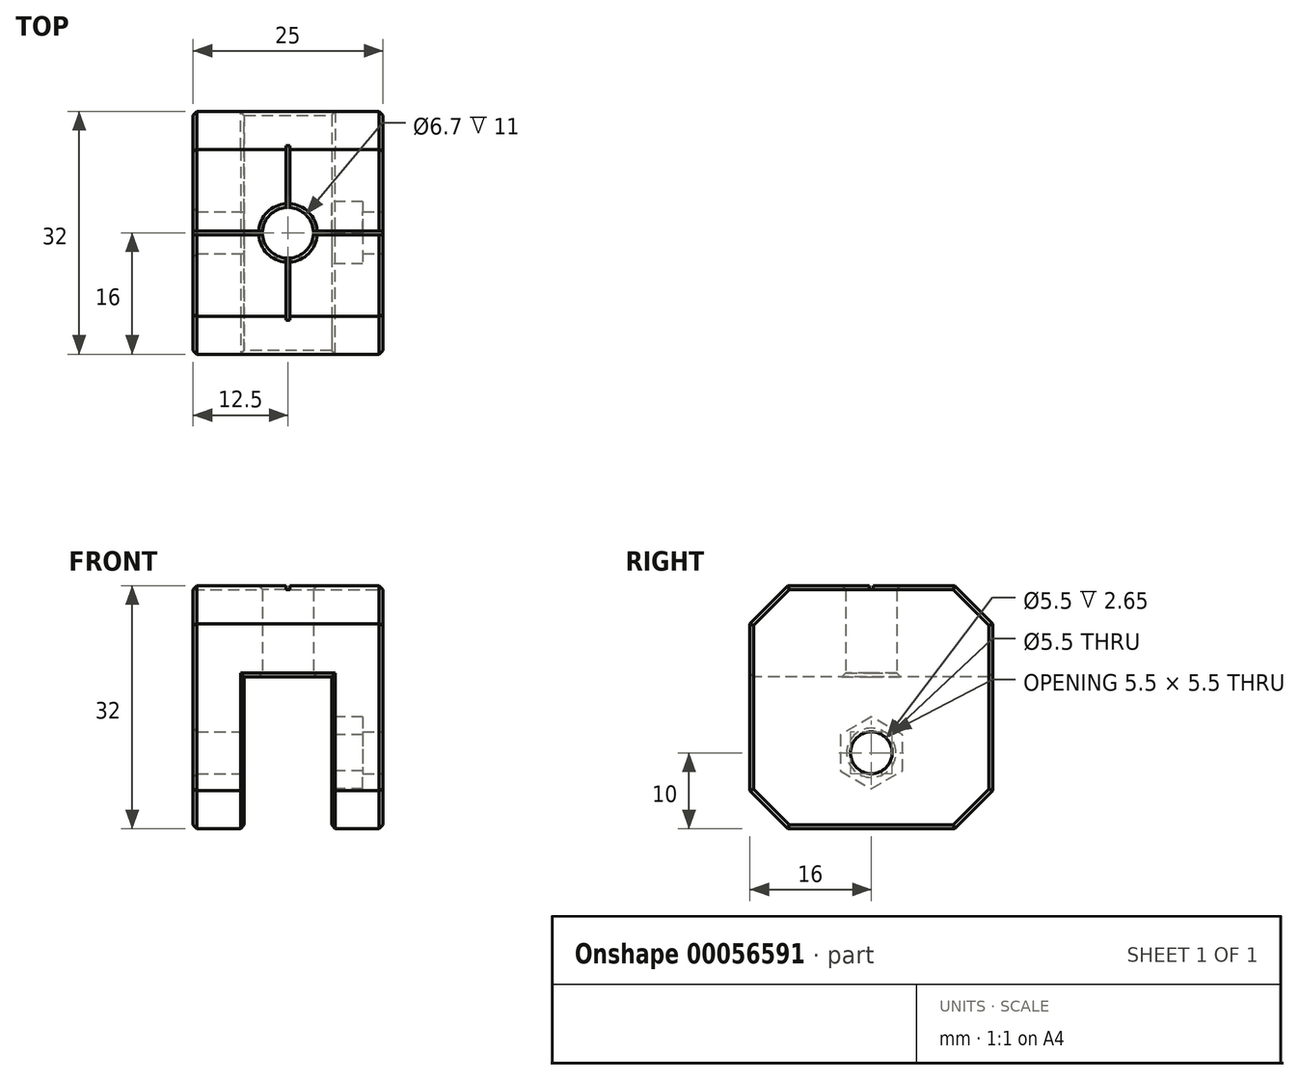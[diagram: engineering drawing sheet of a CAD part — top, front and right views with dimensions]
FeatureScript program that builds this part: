
annotation { "Feature Type Name" : "Feature", "Feature Type Description" : "" }
export const myFeature = defineFeature(function(context is Context, id is Id, definition is map)
    precondition{}
    {
        {
            var Q0;
            Q0=qCreatedBy(makeId("Top.planeOp"),FACE);
            var sketch = newSketch(context, id + "F0", { "sketchPlane" : qUnion([Q0])});
            skCircle(sketch, "E0", {"center": v(0, 0) * mm, "radius": 3.35 * mm});
            skLineSegment(sketch, "E1.bottom", {"start": v(12.5, 16) * mm, "end": v(-12.5, 16) * mm});
            skLineSegment(sketch, "E1.top", {"start": v(12.5, -16) * mm, "end": v(-12.5, -16) * mm});
            skLineSegment(sketch, "E1.left", {"start": v(12.5, 16) * mm, "end": v(12.5, -16) * mm});
            skLineSegment(sketch, "E1.right", {"start": v(-12.5, 16) * mm, "end": v(-12.5, -16) * mm});
            skLineSegment(sketch, "E2", {"start": v(5.75, 16) * mm, "end": v(5.75, -16) * mm});
            skLineSegment(sketch, "E3", {"start": v(-5.75, 16) * mm, "end": v(-5.75, -16) * mm});
            skLineSegment(sketch, "E4", {"start": v(12.5, 0) * mm, "end": v(5.75, 0) * mm, "construction": true});
            skLineSegment(sketch, "E5", {"start": v(5.75, 0) * mm, "end": v(0, 0) * mm, "construction": true});
            skLineSegment(sketch, "E6", {"start": v(-5.75, 0) * mm, "end": v(0, 0) * mm, "construction": true});
            skLineSegment(sketch, "E7", {"start": v(-5.75, 0) * mm, "end": v(-12.5, 0) * mm, "construction": true});
            skSolve(sketch);
        }
        {
            var Q0;
            Q0 = qSketchRegion(id + "F0", true);
            extrude(context, id + "F1", {"entities" : qUnion([Q0]), "depth" : 12 * mm});
        }
        {
            var Q0;
            {var subQ0=sQuery(id+"F0.wireOp",EDGE,"E1.left");Q0=makeQuery(id+"F0.imprint","IMPRINT",FACE,{"disambiguationData":[TD([[makeQuery(id+"F0.imprint","IMPRINT",EDGE,{"derivedFrom":subQ0}),-1.0]])]});}
            var Q1;
            {var subQ0=sQuery(id+"F0.wireOp",EDGE,"E1.right");Q1=makeQuery(id+"F0.imprint","IMPRINT",FACE,{"disambiguationData":[TD([[makeQuery(id+"F0.imprint","IMPRINT",EDGE,{"derivedFrom":subQ0}),1.0]])]});}
            extrude(context, id + "F2", {"entities" : qUnion([Q0, Q1]), "operationType" : NewBodyOperationType.ADD, "oppositeDirection" : true, "depth" : 20 * mm});
        }
        {
            var Q0;
            {var subQ0=sQuery(id+"F0.wireOp",EDGE,"E1.top");Q0=makeQuery(id+"F2.opExtrude","CAP_EDGE",EDGE,{"disambiguationData":[OSD([subQ0]),TDD([makeQuery(id+"F0.imprint","IMPRINT",EDGE,{"disambiguationData":[TD([[makeQuery(id+"F0.imprint","INTERSECT",VERTEX,{"derivedFrom":[subQ0,sQuery(id+"F0.wireOp",EDGE,"E1.right")]}),1.0]])],"derivedFrom":subQ0})])],"isStart":false});}
            var Q1;
            {var subQ0=sQuery(id+"F0.wireOp",EDGE,"E1.top");Q1=makeQuery(id+"F2.opExtrude","CAP_EDGE",EDGE,{"disambiguationData":[OSD([subQ0]),TDD([makeQuery(id+"F0.imprint","IMPRINT",EDGE,{"disambiguationData":[TD([[makeQuery(id+"F0.imprint","INTERSECT",VERTEX,{"derivedFrom":[subQ0,sQuery(id+"F0.wireOp",EDGE,"E1.left")]}),-1.0]])],"derivedFrom":subQ0})])],"isStart":false});}
            var Q2;
            {var subQ0=sQuery(id+"F0.wireOp",EDGE,"E1.bottom");Q2=makeQuery(id+"F2.opExtrude","CAP_EDGE",EDGE,{"disambiguationData":[OSD([subQ0]),TDD([makeQuery(id+"F0.imprint","IMPRINT",EDGE,{"disambiguationData":[TD([[makeQuery(id+"F0.imprint","INTERSECT",VERTEX,{"derivedFrom":[subQ0,sQuery(id+"F0.wireOp",EDGE,"E1.left")]}),-1.0]])],"derivedFrom":subQ0})])],"isStart":false});}
            var Q3;
            {var subQ0=sQuery(id+"F0.wireOp",EDGE,"E1.bottom");Q3=makeQuery(id+"F2.opExtrude","CAP_EDGE",EDGE,{"disambiguationData":[OSD([subQ0]),TDD([makeQuery(id+"F0.imprint","IMPRINT",EDGE,{"disambiguationData":[TD([[makeQuery(id+"F0.imprint","INTERSECT",VERTEX,{"derivedFrom":[subQ0,sQuery(id+"F0.wireOp",EDGE,"E1.right")]}),1.0]])],"derivedFrom":subQ0})])],"isStart":false});}
            chamfer(context, id + "F3", {"entities" : qUnion([Q0, Q1, Q2, Q3]), "width" : 5 * mm, "tangentPropagation" : true});
        }
        {
            var Q0;
            Q0=makeQuery(id+"F1.opExtrude","CAP_EDGE",EDGE,{"disambiguationData":[OSD([sQuery(id+"F0.wireOp",EDGE,"E1.top")])],"isStart":false});
            var Q1;
            Q1=makeQuery(id+"F1.opExtrude","CAP_EDGE",EDGE,{"disambiguationData":[OSD([sQuery(id+"F0.wireOp",EDGE,"E1.bottom")])],"isStart":false});
            chamfer(context, id + "F4", {"entities" : qUnion([Q0, Q1]), "width" : 5 * mm, "tangentPropagation" : true});
        }
        {
            var Q0;
            {var subQ0=sQuery(id+"F0.wireOp",EDGE,"E1.right");Q0=makeQuery(id+"F2.boolean.opBoolean","MERGE",FACE,{"derivedFrom":[makeQuery(id+"F1.opExtrude","SWEPT_FACE",FACE,{"disambiguationData":[OSD([subQ0])]}),makeQuery(id+"F2.opExtrude","SWEPT_FACE",FACE,{"disambiguationData":[OSD([subQ0])]})]});}
            var sketch = newSketch(context, id + "F5", { "sketchPlane" : qUnion([Q0])});
            skLineSegment(sketch, "E8", {"start": v(16, -10) * mm, "end": v(-16, -10) * mm});
            skLineSegment(sketch, "E9", {"start": v(0, -20) * mm, "end": v(0, -10) * mm});
            skLineSegment(sketch, "E10.0", {"start": v(-16, 0) * mm, "end": v(16, 0) * mm});
            skSolve(sketch);
        }
        {
            var Q0;
            Q0=sQuery(id+"F5.wireOp",VERTEX,"E9.end");
            var Q1;
            Q1=makeQuery(id+"F1.opExtrude","SWEPT_BODY",BODY,{"disambiguationData":[OSD([sQuery(id+"F0.wireOp",EDGE,"E0"),sQuery(id+"F0.wireOp",EDGE,"E1.bottom"),sQuery(id+"F0.wireOp",EDGE,"E1.top"),sQuery(id+"F0.wireOp",EDGE,"E1.left"),sQuery(id+"F0.wireOp",EDGE,"E1.right")])]});
            hole(context, id + "F6", {"style" : HoleStyle.SIMPLE, "endStyle" : HoleEndStyle.THROUGH, "standardTappedOrClearance" : lookupTablePath({ "standard" : "ISO", "fit" : "Normal", "size" : "M5", "type" : "Clearance" }), "standardBlindInLast" : lookupTablePath({ "fit" : "Standard", "standard" : "ISO", "size" : "M5", "type" : "Clearance" }), "holeDiameter" : 5.5 * mm, "tappedDepth" : 3 * mm, "tapClearance" : 3, "startFromSketch" : true, "locations" : qUnion([Q0]), "scope" : qUnion([Q1])});
        }
        {
            var Q0;
            Q0=makeQuery(id+"F2.opExtrude","SWEPT_FACE",FACE,{"disambiguationData":[OSD([sQuery(id+"F0.wireOp",EDGE,"E2")])]});
            var sketch = newSketch(context, id + "F7", { "sketchPlane" : qUnion([Q0])});
            skCircle(sketch, "E11.cCircle", {"center": v(0, -10) * mm, "radius": 4.1 * mm, "construction": true});
            skLineSegment(sketch, "E11.0", {"start": v(4.1, -7.63) * mm, "end": v(4.1, -12.37) * mm});
            skLineSegment(sketch, "E11.1", {"start": v(4.1, -12.37) * mm, "end": v(0, -14.73) * mm});
            skLineSegment(sketch, "E11.2", {"start": v(0, -14.73) * mm, "end": v(-4.1, -12.37) * mm});
            skLineSegment(sketch, "E11.3", {"start": v(-4.1, -12.37) * mm, "end": v(-4.1, -7.63) * mm});
            skLineSegment(sketch, "E11.4", {"start": v(-4.1, -7.63) * mm, "end": v(0, -5.27) * mm});
            skLineSegment(sketch, "E11.5", {"start": v(0, -5.27) * mm, "end": v(4.1, -7.63) * mm});
            skPoint(sketch, "E11.0.midPoint", {"position": v(4.1, -10) * mm});
            skSolve(sketch);
        }
        {
            var Q0;
            Q0 = qSketchRegion(id + "F7", true);
            extrude(context, id + "F8", {"entities" : qUnion([Q0]), "operationType" : NewBodyOperationType.REMOVE, "oppositeDirection" : true, "depth" : 4.1 * mm});
        }
        {
            var Q0;
            Q0=makeQuery(id+"F1.opExtrude","CAP_FACE",FACE,{"disambiguationData":[OSD([sQuery(id+"F0.wireOp",EDGE,"E0"),sQuery(id+"F0.wireOp",EDGE,"E1.bottom"),sQuery(id+"F0.wireOp",EDGE,"E1.top"),sQuery(id+"F0.wireOp",EDGE,"E1.left"),sQuery(id+"F0.wireOp",EDGE,"E1.right")])],"isStart":false});
            var sketch = newSketch(context, id + "F9", { "sketchPlane" : qUnion([Q0])});
            skLineSegment(sketch, "E12.bottom", {"start": v(-12.5, -0.25) * mm, "end": v(12.5, -0.25) * mm});
            skLineSegment(sketch, "E12.top", {"start": v(-12.5, 0.25) * mm, "end": v(12.5, 0.25) * mm});
            skLineSegment(sketch, "E12.left", {"start": v(-12.5, -0.25) * mm, "end": v(-12.5, 0.25) * mm});
            skLineSegment(sketch, "E12.right", {"start": v(12.5, -0.25) * mm, "end": v(12.5, 0.25) * mm});
            skPoint(sketch, "E12.middle", {"position": v(0, 0) * mm});
            skLineSegment(sketch, "E13.0", {"start": v(12.5, -16) * mm, "end": v(-12.5, -16) * mm, "construction": true});
            skLineSegment(sketch, "E14.0", {"start": v(-12.5, 16) * mm, "end": v(12.5, 16) * mm, "construction": true});
            skLineSegment(sketch, "E15.bottom", {"start": v(0.25, 16) * mm, "end": v(-0.25, 16) * mm});
            skLineSegment(sketch, "E15.top", {"start": v(0.25, -16) * mm, "end": v(-0.25, -16) * mm});
            skLineSegment(sketch, "E15.left", {"start": v(0.25, 16) * mm, "end": v(0.25, -16) * mm});
            skLineSegment(sketch, "E15.right", {"start": v(-0.25, 16) * mm, "end": v(-0.25, -16) * mm});
            skSolve(sketch);
        }
        {
            var Q0;
            Q0=makeQuery(id+"F1.opExtrude","CAP_EDGE",EDGE,{"disambiguationData":[OSD([sQuery(id+"F0.wireOp",EDGE,"E1.left")])],"isStart":false});
            var Q1;
            {var subQ0=sQuery(id+"F0.wireOp",EDGE,"E1.left");Q1=makeQuery(id+"F4.opChamfer","BLEND_EDGE",EDGE,{"blendedFrom":[makeQuery(id+"F1.opExtrude","CAP_EDGE",EDGE,{"disambiguationData":[OSD([sQuery(id+"F0.wireOp",EDGE,"E1.top")])],"isStart":false}),makeQuery(id+"F2.boolean.opBoolean","MERGE",FACE,{"derivedFrom":[makeQuery(id+"F1.opExtrude","SWEPT_FACE",FACE,{"disambiguationData":[OSD([subQ0])]}),makeQuery(id+"F2.opExtrude","SWEPT_FACE",FACE,{"disambiguationData":[OSD([subQ0])]})]})],"blendedInto":[makeQuery(id+"F2.boolean.opBoolean","MERGE",FACE,{"derivedFrom":[makeQuery(id+"F1.opExtrude","SWEPT_FACE",FACE,{"disambiguationData":[OSD([subQ0])]}),makeQuery(id+"F2.opExtrude","SWEPT_FACE",FACE,{"disambiguationData":[OSD([subQ0])]})]})]});}
            var Q2;
            {var subQ0=sQuery(id+"F0.wireOp",EDGE,"E1.left");var subQ1=sQuery(id+"F0.wireOp",EDGE,"E1.top");Q2=makeQuery(id+"F2.boolean.opBoolean","MERGE",EDGE,{"derivedFrom":[makeQuery(id+"F1.opExtrude","SWEPT_EDGE",EDGE,{"disambiguationData":[OSD([subQ1,subQ0])]}),makeQuery(id+"F2.opExtrude","SWEPT_EDGE",EDGE,{"disambiguationData":[OSD([subQ1,subQ0])]})]});}
            var Q3;
            {var subQ0=sQuery(id+"F0.wireOp",EDGE,"E1.left");var subQ1=sQuery(id+"F0.wireOp",EDGE,"E1.top");Q3=makeQuery(id+"F3.opChamfer","BLEND_EDGE",EDGE,{"blendedFrom":[makeQuery(id+"F2.opExtrude","CAP_EDGE",EDGE,{"disambiguationData":[OSD([subQ1]),TDD([makeQuery(id+"F0.imprint","IMPRINT",EDGE,{"disambiguationData":[TD([[makeQuery(id+"F0.imprint","INTERSECT",VERTEX,{"derivedFrom":[subQ1,subQ0]}),-1.0]])],"derivedFrom":subQ1})])],"isStart":false}),makeQuery(id+"F2.boolean.opBoolean","MERGE",FACE,{"derivedFrom":[makeQuery(id+"F1.opExtrude","SWEPT_FACE",FACE,{"disambiguationData":[OSD([subQ0])]}),makeQuery(id+"F2.opExtrude","SWEPT_FACE",FACE,{"disambiguationData":[OSD([subQ0])]})]})],"blendedInto":[makeQuery(id+"F2.boolean.opBoolean","MERGE",FACE,{"derivedFrom":[makeQuery(id+"F1.opExtrude","SWEPT_FACE",FACE,{"disambiguationData":[OSD([subQ0])]}),makeQuery(id+"F2.opExtrude","SWEPT_FACE",FACE,{"disambiguationData":[OSD([subQ0])]})]})]});}
            var Q4;
            Q4=makeQuery(id+"F2.opExtrude","CAP_EDGE",EDGE,{"disambiguationData":[OSD([sQuery(id+"F0.wireOp",EDGE,"E1.left")])],"isStart":false});
            var Q5;
            {var subQ0=sQuery(id+"F0.wireOp",EDGE,"E1.left");var subQ1=sQuery(id+"F0.wireOp",EDGE,"E1.bottom");Q5=makeQuery(id+"F3.opChamfer","BLEND_EDGE",EDGE,{"blendedFrom":[makeQuery(id+"F2.opExtrude","CAP_EDGE",EDGE,{"disambiguationData":[OSD([subQ1]),TDD([makeQuery(id+"F0.imprint","IMPRINT",EDGE,{"disambiguationData":[TD([[makeQuery(id+"F0.imprint","INTERSECT",VERTEX,{"derivedFrom":[subQ1,subQ0]}),-1.0]])],"derivedFrom":subQ1})])],"isStart":false}),makeQuery(id+"F2.boolean.opBoolean","MERGE",FACE,{"derivedFrom":[makeQuery(id+"F1.opExtrude","SWEPT_FACE",FACE,{"disambiguationData":[OSD([subQ0])]}),makeQuery(id+"F2.opExtrude","SWEPT_FACE",FACE,{"disambiguationData":[OSD([subQ0])]})]})],"blendedInto":[makeQuery(id+"F2.boolean.opBoolean","MERGE",FACE,{"derivedFrom":[makeQuery(id+"F1.opExtrude","SWEPT_FACE",FACE,{"disambiguationData":[OSD([subQ0])]}),makeQuery(id+"F2.opExtrude","SWEPT_FACE",FACE,{"disambiguationData":[OSD([subQ0])]})]})]});}
            var Q6;
            {var subQ0=sQuery(id+"F0.wireOp",EDGE,"E1.left");var subQ1=sQuery(id+"F0.wireOp",EDGE,"E1.bottom");Q6=makeQuery(id+"F2.boolean.opBoolean","MERGE",EDGE,{"derivedFrom":[makeQuery(id+"F1.opExtrude","SWEPT_EDGE",EDGE,{"disambiguationData":[OSD([subQ1,subQ0])]}),makeQuery(id+"F2.opExtrude","SWEPT_EDGE",EDGE,{"disambiguationData":[OSD([subQ1,subQ0])]})]});}
            var Q7;
            {var subQ0=sQuery(id+"F0.wireOp",EDGE,"E1.left");Q7=makeQuery(id+"F4.opChamfer","BLEND_EDGE",EDGE,{"blendedFrom":[makeQuery(id+"F1.opExtrude","CAP_EDGE",EDGE,{"disambiguationData":[OSD([sQuery(id+"F0.wireOp",EDGE,"E1.bottom")])],"isStart":false}),makeQuery(id+"F2.boolean.opBoolean","MERGE",FACE,{"derivedFrom":[makeQuery(id+"F1.opExtrude","SWEPT_FACE",FACE,{"disambiguationData":[OSD([subQ0])]}),makeQuery(id+"F2.opExtrude","SWEPT_FACE",FACE,{"disambiguationData":[OSD([subQ0])]})]})],"blendedInto":[makeQuery(id+"F2.boolean.opBoolean","MERGE",FACE,{"derivedFrom":[makeQuery(id+"F1.opExtrude","SWEPT_FACE",FACE,{"disambiguationData":[OSD([subQ0])]}),makeQuery(id+"F2.opExtrude","SWEPT_FACE",FACE,{"disambiguationData":[OSD([subQ0])]})]})]});}
            var Q8;
            {var subQ0=sQuery(id+"F0.wireOp",EDGE,"E1.right");Q8=makeQuery(id+"F2.boolean.opBoolean","MERGE",FACE,{"derivedFrom":[makeQuery(id+"F1.opExtrude","SWEPT_FACE",FACE,{"disambiguationData":[OSD([subQ0])]}),makeQuery(id+"F2.opExtrude","SWEPT_FACE",FACE,{"disambiguationData":[OSD([subQ0])]})]});}
            var Q9;
            Q9=makeQuery(id+"F1.opExtrude","CAP_EDGE",EDGE,{"disambiguationData":[OSD([sQuery(id+"F0.wireOp",EDGE,"E1.bottom")])],"isStart":true});
            var Q10;
            Q10=makeQuery(id+"F1.opExtrude","CAP_EDGE",EDGE,{"disambiguationData":[OSD([sQuery(id+"F0.wireOp",EDGE,"E1.top")])],"isStart":true});
            var Q11;
            Q11=makeQuery(id+"F2.opExtrude","SWEPT_EDGE",EDGE,{"disambiguationData":[OSD([sQuery(id+"F0.wireOp",EDGE,"E1.top"),sQuery(id+"F0.wireOp",EDGE,"E2")])]});
            var Q12;
            {var subQ0=sQuery(id+"F0.wireOp",EDGE,"E2");var subQ1=sQuery(id+"F0.wireOp",EDGE,"E1.top");Q12=makeQuery(id+"F3.opChamfer","BLEND_EDGE",EDGE,{"blendedFrom":[makeQuery(id+"F2.opExtrude","CAP_EDGE",EDGE,{"disambiguationData":[OSD([subQ1]),TDD([makeQuery(id+"F0.imprint","IMPRINT",EDGE,{"disambiguationData":[TD([[makeQuery(id+"F0.imprint","INTERSECT",VERTEX,{"derivedFrom":[subQ1,sQuery(id+"F0.wireOp",EDGE,"E1.left")]}),-1.0]])],"derivedFrom":subQ1})])],"isStart":false}),makeQuery(id+"F2.opExtrude","SWEPT_FACE",FACE,{"disambiguationData":[OSD([subQ0])]})],"blendedInto":[makeQuery(id+"F2.opExtrude","SWEPT_FACE",FACE,{"disambiguationData":[OSD([subQ0])]})]});}
            var Q13;
            Q13=makeQuery(id+"F2.opExtrude","CAP_EDGE",EDGE,{"disambiguationData":[OSD([sQuery(id+"F0.wireOp",EDGE,"E2")])],"isStart":false});
            var Q14;
            {var subQ0=sQuery(id+"F0.wireOp",EDGE,"E2");var subQ1=sQuery(id+"F0.wireOp",EDGE,"E1.bottom");Q14=makeQuery(id+"F3.opChamfer","BLEND_EDGE",EDGE,{"blendedFrom":[makeQuery(id+"F2.opExtrude","CAP_EDGE",EDGE,{"disambiguationData":[OSD([subQ1]),TDD([makeQuery(id+"F0.imprint","IMPRINT",EDGE,{"disambiguationData":[TD([[makeQuery(id+"F0.imprint","INTERSECT",VERTEX,{"derivedFrom":[subQ1,sQuery(id+"F0.wireOp",EDGE,"E1.left")]}),-1.0]])],"derivedFrom":subQ1})])],"isStart":false}),makeQuery(id+"F2.opExtrude","SWEPT_FACE",FACE,{"disambiguationData":[OSD([subQ0])]})],"blendedInto":[makeQuery(id+"F2.opExtrude","SWEPT_FACE",FACE,{"disambiguationData":[OSD([subQ0])]})]});}
            var Q15;
            Q15=makeQuery(id+"F2.opExtrude","SWEPT_EDGE",EDGE,{"disambiguationData":[OSD([sQuery(id+"F0.wireOp",EDGE,"E1.bottom"),sQuery(id+"F0.wireOp",EDGE,"E2")])]});
            var Q16;
            Q16=makeQuery(id+"F2.opExtrude","SWEPT_EDGE",EDGE,{"disambiguationData":[OSD([sQuery(id+"F0.wireOp",EDGE,"E1.bottom"),sQuery(id+"F0.wireOp",EDGE,"E3")])]});
            var Q17;
            {var subQ0=sQuery(id+"F0.wireOp",EDGE,"E3");var subQ1=sQuery(id+"F0.wireOp",EDGE,"E1.bottom");Q17=makeQuery(id+"F3.opChamfer","BLEND_EDGE",EDGE,{"blendedFrom":[makeQuery(id+"F2.opExtrude","CAP_EDGE",EDGE,{"disambiguationData":[OSD([subQ1]),TDD([makeQuery(id+"F0.imprint","IMPRINT",EDGE,{"disambiguationData":[TD([[makeQuery(id+"F0.imprint","INTERSECT",VERTEX,{"derivedFrom":[subQ1,sQuery(id+"F0.wireOp",EDGE,"E1.right")]}),1.0]])],"derivedFrom":subQ1})])],"isStart":false}),makeQuery(id+"F2.opExtrude","SWEPT_FACE",FACE,{"disambiguationData":[OSD([subQ0])]})],"blendedInto":[makeQuery(id+"F2.opExtrude","SWEPT_FACE",FACE,{"disambiguationData":[OSD([subQ0])]})]});}
            var Q18;
            Q18=makeQuery(id+"F2.opExtrude","CAP_EDGE",EDGE,{"disambiguationData":[OSD([sQuery(id+"F0.wireOp",EDGE,"E3")])],"isStart":false});
            var Q19;
            {var subQ0=sQuery(id+"F0.wireOp",EDGE,"E3");var subQ1=sQuery(id+"F0.wireOp",EDGE,"E1.top");Q19=makeQuery(id+"F3.opChamfer","BLEND_EDGE",EDGE,{"blendedFrom":[makeQuery(id+"F2.opExtrude","CAP_EDGE",EDGE,{"disambiguationData":[OSD([subQ1]),TDD([makeQuery(id+"F0.imprint","IMPRINT",EDGE,{"disambiguationData":[TD([[makeQuery(id+"F0.imprint","INTERSECT",VERTEX,{"derivedFrom":[subQ1,sQuery(id+"F0.wireOp",EDGE,"E1.right")]}),1.0]])],"derivedFrom":subQ1})])],"isStart":false}),makeQuery(id+"F2.opExtrude","SWEPT_FACE",FACE,{"disambiguationData":[OSD([subQ0])]})],"blendedInto":[makeQuery(id+"F2.opExtrude","SWEPT_FACE",FACE,{"disambiguationData":[OSD([subQ0])]})]});}
            var Q20;
            Q20=makeQuery(id+"F2.opExtrude","SWEPT_EDGE",EDGE,{"disambiguationData":[OSD([sQuery(id+"F0.wireOp",EDGE,"E1.top"),sQuery(id+"F0.wireOp",EDGE,"E3")])]});
            var Q21;
            Q21=makeQuery(id+"F1.opExtrude","CAP_EDGE",EDGE,{"disambiguationData":[OSD([sQuery(id+"F0.wireOp",EDGE,"E0")])],"isStart":false});
            var Q22;
            Q22=makeQuery(id+"F1.opExtrude","CAP_EDGE",EDGE,{"disambiguationData":[OSD([sQuery(id+"F0.wireOp",EDGE,"E0")])],"isStart":true});
            var Q23;
            {var subQ0=sQuery(id+"F0.wireOp",EDGE,"E1.left");Q23=makeQuery(id+"F6.hole-0.boolean.opBoolean","INTERSECT",EDGE,{"derivedFrom":[makeQuery(id+"F2.boolean.opBoolean","MERGE",FACE,{"derivedFrom":[makeQuery(id+"F1.opExtrude","SWEPT_FACE",FACE,{"disambiguationData":[OSD([subQ0])]}),makeQuery(id+"F2.opExtrude","SWEPT_FACE",FACE,{"disambiguationData":[OSD([subQ0])]})]}),makeQuery(id+"F6.hole-0.opRevolve","SWEPT_FACE",FACE,{"disambiguationData":[OSD([sQuery(id+"F6.hole-0.sketch.wireOp",EDGE,"core_line_2")])]})]});}
            chamfer(context, id + "F10", {"entities" : qUnion([Q0, Q1, Q2, Q3, Q4, Q5, Q6, Q7, Q8, Q9, Q10, Q11, Q12, Q13, Q14, Q15, Q16, Q17, Q18, Q19, Q20, Q21, Q22, Q23]), "width" : 0.5 * mm, "tangentPropagation" : true});
        }
        {
            var Q0;
            Q0 = qSketchRegion(id + "F9", true);
            extrude(context, id + "F11", {"entities" : qUnion([Q0]), "operationType" : NewBodyOperationType.REMOVE, "oppositeDirection" : true, "depth" : .5 * mm});
        }
    });
